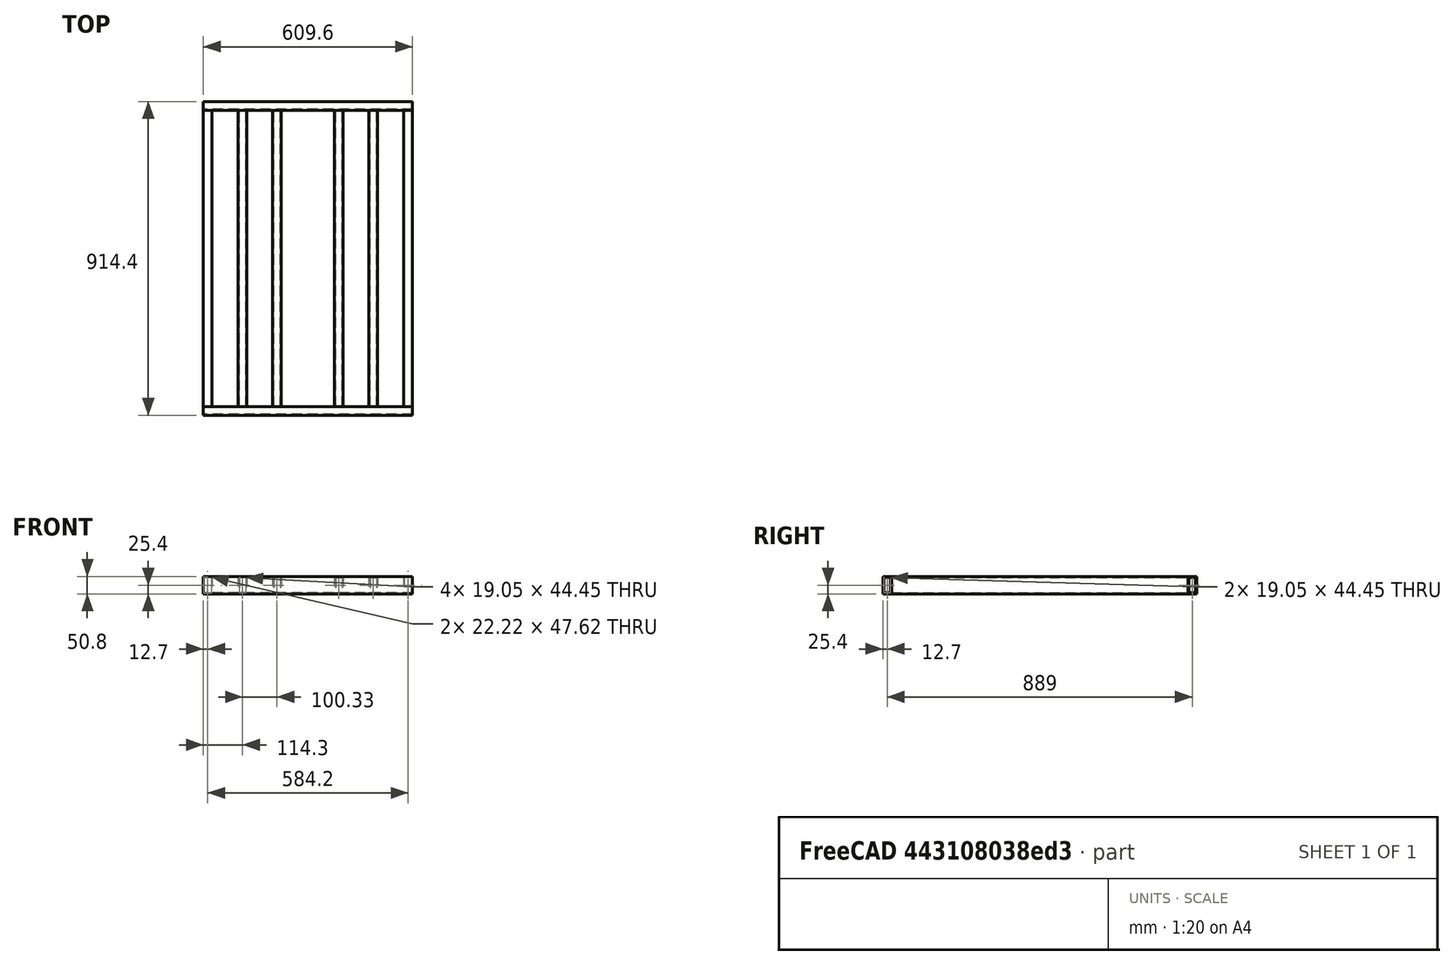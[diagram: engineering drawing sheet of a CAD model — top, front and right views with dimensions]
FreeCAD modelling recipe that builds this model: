
FCSTD DOCUMENT  (FreeCAD 0.20R29177 +426 (Git))
Label: FRC-ChassisMaker
License: All rights reserved
LicenseURL: http://en.wikipedia.org/wiki/All_rights_reserved
objects: Part::Plane×16, Part::Cut×8, Part::FeaturePython×8, Part::Extrusion×8, Part::MultiFuse×2, Part::Mirroring×1
note: 43 computed .brp shape members not serialized (recipe doc carries the construction recipe); baked Part::Feature solids carry a one-line shape summary decoded from their .brp

FEATURE [Part::Plane] square
  AttacherType = Attacher::AttachEngine3D
  Length = 25.4
  Placement = pos=(-12.7,-25.4,0) rot=(0,0,1;0rad)
  Width = 50.8
FEATURE [Part::Plane] square001
  AttacherType = Attacher::AttachEngine3D
  Length = 19.05
  Placement = pos=(-9.525,-22.225,0) rot=(0,0,1;0rad)
  Width = 44.45
FEATURE [Part::Cut] difference
  Base = -> square
  Tool = -> square001
FEATURE [Part::FeaturePython] RefineLinearExtrude  # WARN: FeaturePython — macro-defined, semantics opaque (R4)
  Base = -> difference
FEATURE [Part::Extrusion] LinearExtrude
  Base = -> RefineLinearExtrude
  Dir = (0,0,863.6)
  DirMode = 0
  FaceMakerClass = Part::FaceMakerBullseye
  LengthFwd = 0
  LengthRev = 0
  Placement = pos=(90.17,25.4,25.4) rot=(-1,0,0;1.5708rad)
  Solid = false
  Symmetric = false
FEATURE [Part::Plane] square002
  AttacherType = Attacher::AttachEngine3D
  Length = 25.4
  Placement = pos=(-12.7,-25.4,0) rot=(0,0,1;0rad)
  Width = 50.8
FEATURE [Part::Plane] square003
  AttacherType = Attacher::AttachEngine3D
  Length = 19.05
  Placement = pos=(-9.525,-22.225,0) rot=(0,0,1;0rad)
  Width = 44.45
FEATURE [Part::Cut] difference001
  Base = -> square002
  Tool = -> square003
FEATURE [Part::FeaturePython] RefineLinearExtrude001  # WARN: FeaturePython — macro-defined, semantics opaque (R4)
  Base = -> difference001
FEATURE [Part::Extrusion] LinearExtrude001
  Base = -> RefineLinearExtrude001
  Dir = (0,0,863.6)
  DirMode = 0
  FaceMakerClass = Part::FaceMakerBullseye
  LengthFwd = 0
  LengthRev = 0
  Placement = pos=(190.5,25.4,25.4) rot=(-1,0,0;1.5708rad)
  Solid = false
  Symmetric = false
FEATURE [Part::Plane] square004
  AttacherType = Attacher::AttachEngine3D
  Length = 25.4
  Placement = pos=(-12.7,-25.4,0) rot=(0,0,1;0rad)
  Width = 50.8
FEATURE [Part::Plane] square005
  AttacherType = Attacher::AttachEngine3D
  Length = 22.225
  Placement = pos=(-11.1125,-23.8125,0) rot=(0,0,1;0rad)
  Width = 47.625
FEATURE [Part::Cut] difference002
  Base = -> square004
  Tool = -> square005
FEATURE [Part::FeaturePython] RefineLinearExtrude002  # WARN: FeaturePython — macro-defined, semantics opaque (R4)
  Base = -> difference002
FEATURE [Part::Extrusion] LinearExtrude002
  Base = -> RefineLinearExtrude002
  Dir = (0,0,863.6)
  DirMode = 0
  FaceMakerClass = Part::FaceMakerBullseye
  LengthFwd = 0
  LengthRev = 0
  Placement = pos=(292.1,25.4,25.4) rot=(-1,0,0;1.5708rad)
  Solid = false
  Symmetric = false
FEATURE [Part::MultiFuse] Group
  Shapes = -> [LinearExtrude,LinearExtrude001,LinearExtrude002]
FEATURE [Part::Plane] square006
  AttacherType = Attacher::AttachEngine3D
  Length = 25.4
  Placement = pos=(-12.7,-25.4,0) rot=(0,0,1;0rad)
  Width = 50.8
FEATURE [Part::Plane] square007
  AttacherType = Attacher::AttachEngine3D
  Length = 19.05
  Placement = pos=(-9.525,-22.225,0) rot=(0,0,1;0rad)
  Width = 44.45
FEATURE [Part::Cut] difference003
  Base = -> square006
  Tool = -> square007
FEATURE [Part::FeaturePython] RefineLinearExtrude003  # WARN: FeaturePython — macro-defined, semantics opaque (R4)
  Base = -> difference003
FEATURE [Part::Extrusion] LinearExtrude003
  Base = -> RefineLinearExtrude003
  Dir = (0,0,863.6)
  DirMode = 0
  FaceMakerClass = Part::FaceMakerBullseye
  LengthFwd = 0
  LengthRev = 0
  Placement = pos=(90.17,25.4,25.4) rot=(-1,0,0;1.5708rad)
  Solid = false
  Symmetric = false
FEATURE [Part::Plane] square008
  AttacherType = Attacher::AttachEngine3D
  Length = 25.4
  Placement = pos=(-12.7,-25.4,0) rot=(0,0,1;0rad)
  Width = 50.8
FEATURE [Part::Plane] square009
  AttacherType = Attacher::AttachEngine3D
  Length = 19.05
  Placement = pos=(-9.525,-22.225,0) rot=(0,0,1;0rad)
  Width = 44.45
FEATURE [Part::Cut] difference004
  Base = -> square008
  Tool = -> square009
FEATURE [Part::FeaturePython] RefineLinearExtrude004  # WARN: FeaturePython — macro-defined, semantics opaque (R4)
  Base = -> difference004
FEATURE [Part::Extrusion] LinearExtrude004
  Base = -> RefineLinearExtrude004
  Dir = (0,0,863.6)
  DirMode = 0
  FaceMakerClass = Part::FaceMakerBullseye
  LengthFwd = 0
  LengthRev = 0
  Placement = pos=(190.5,25.4,25.4) rot=(-1,0,0;1.5708rad)
  Solid = false
  Symmetric = false
FEATURE [Part::Plane] square010
  AttacherType = Attacher::AttachEngine3D
  Length = 25.4
  Placement = pos=(-12.7,-25.4,0) rot=(0,0,1;0rad)
  Width = 50.8
FEATURE [Part::Plane] square011
  AttacherType = Attacher::AttachEngine3D
  Length = 22.225
  Placement = pos=(-11.1125,-23.8125,0) rot=(0,0,1;0rad)
  Width = 47.625
FEATURE [Part::Cut] difference005
  Base = -> square010
  Tool = -> square011
FEATURE [Part::FeaturePython] RefineLinearExtrude005  # WARN: FeaturePython — macro-defined, semantics opaque (R4)
  Base = -> difference005
FEATURE [Part::Extrusion] LinearExtrude005
  Base = -> RefineLinearExtrude005
  Dir = (0,0,863.6)
  DirMode = 0
  FaceMakerClass = Part::FaceMakerBullseye
  LengthFwd = 0
  LengthRev = 0
  Placement = pos=(292.1,25.4,25.4) rot=(-1,0,0;1.5708rad)
  Solid = false
  Symmetric = false
FEATURE [Part::MultiFuse] Group001
  Shapes = -> [LinearExtrude003,LinearExtrude004,LinearExtrude005]
FEATURE [Part::Mirroring] mirr_Group001  label="mirrored Group001"
  Base = (0,0,0)
  Normal = (1,0,0)
  Source = -> Group001
FEATURE [Part::Plane] square012
  AttacherType = Attacher::AttachEngine3D
  Length = 25.4
  Placement = pos=(-12.7,-25.4,0) rot=(0,0,1;0rad)
  Width = 50.8
FEATURE [Part::Plane] square013
  AttacherType = Attacher::AttachEngine3D
  Length = 19.05
  Placement = pos=(-9.525,-22.225,0) rot=(0,0,1;0rad)
  Width = 44.45
FEATURE [Part::Cut] difference006
  Base = -> square012
  Tool = -> square013
FEATURE [Part::FeaturePython] RefineLinearExtrude006  # WARN: FeaturePython — macro-defined, semantics opaque (R4)
  Base = -> difference006
FEATURE [Part::Extrusion] LinearExtrude006
  Base = -> RefineLinearExtrude006
  Dir = (0,0,609.6)
  DirMode = 0
  FaceMakerClass = Part::FaceMakerBullseye
  LengthFwd = 0
  LengthRev = 0
  Placement = pos=(304.8,12.7,25.4) rot=(-0.57735,-0.57735,0.57735;2.0944rad)
  Solid = false
  Symmetric = false
FEATURE [Part::Plane] square014
  AttacherType = Attacher::AttachEngine3D
  Length = 25.4
  Placement = pos=(-12.7,-25.4,0) rot=(0,0,1;0rad)
  Width = 50.8
FEATURE [Part::Plane] square015
  AttacherType = Attacher::AttachEngine3D
  Length = 19.05
  Placement = pos=(-9.525,-22.225,0) rot=(0,0,1;0rad)
  Width = 44.45
FEATURE [Part::Cut] difference007
  Base = -> square014
  Tool = -> square015
FEATURE [Part::FeaturePython] RefineLinearExtrude007  # WARN: FeaturePython — macro-defined, semantics opaque (R4)
  Base = -> difference007
FEATURE [Part::Extrusion] LinearExtrude007
  Base = -> RefineLinearExtrude007
  Dir = (0,0,609.6)
  DirMode = 0
  FaceMakerClass = Part::FaceMakerBullseye
  LengthFwd = 0
  LengthRev = 0
  Placement = pos=(304.8,901.7,25.4) rot=(-0.57735,-0.57735,0.57735;2.0944rad)
  Solid = false
  Symmetric = false
